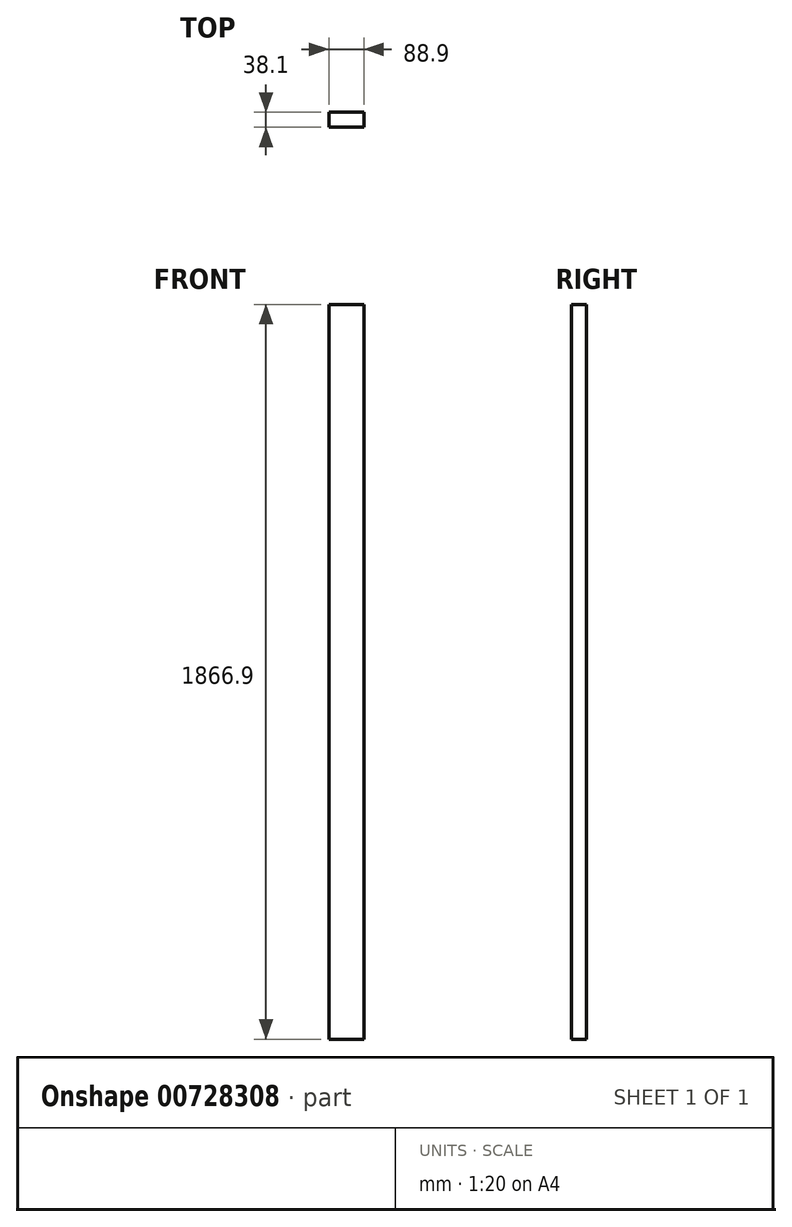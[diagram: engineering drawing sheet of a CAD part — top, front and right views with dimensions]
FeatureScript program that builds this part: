
annotation { "Feature Type Name" : "Feature", "Feature Type Description" : "" }
export const myFeature = defineFeature(function(context is Context, id is Id, definition is map)
    precondition{}
    {
        {
            var Q0;
            Q0=qCreatedBy(makeId("Front.planeOp"),FACE);
            var sketch = newSketch(context, id + "F0", { "sketchPlane" : qUnion([Q0])});
            skLineSegment(sketch, "E0.bottom", {"start": v(44.45, -933.45) * mm, "end": v(-44.45, -933.45) * mm});
            skLineSegment(sketch, "E0.top", {"start": v(44.45, 933.45) * mm, "end": v(-44.45, 933.45) * mm});
            skLineSegment(sketch, "E0.left", {"start": v(44.45, -933.45) * mm, "end": v(44.45, 933.45) * mm});
            skLineSegment(sketch, "E0.right", {"start": v(-44.45, -933.45) * mm, "end": v(-44.45, 933.45) * mm});
            skPoint(sketch, "E0.middle", {"position": v(0, 0) * mm});
            skSolve(sketch);
        }
        {
            var Q0;
            Q0=qSketchRegion(id+"F0",true);
            extrude(context, id + "F1", {"entities" : qUnion([Q0]), "depth" : 38.1 * mm});
        }
    });
